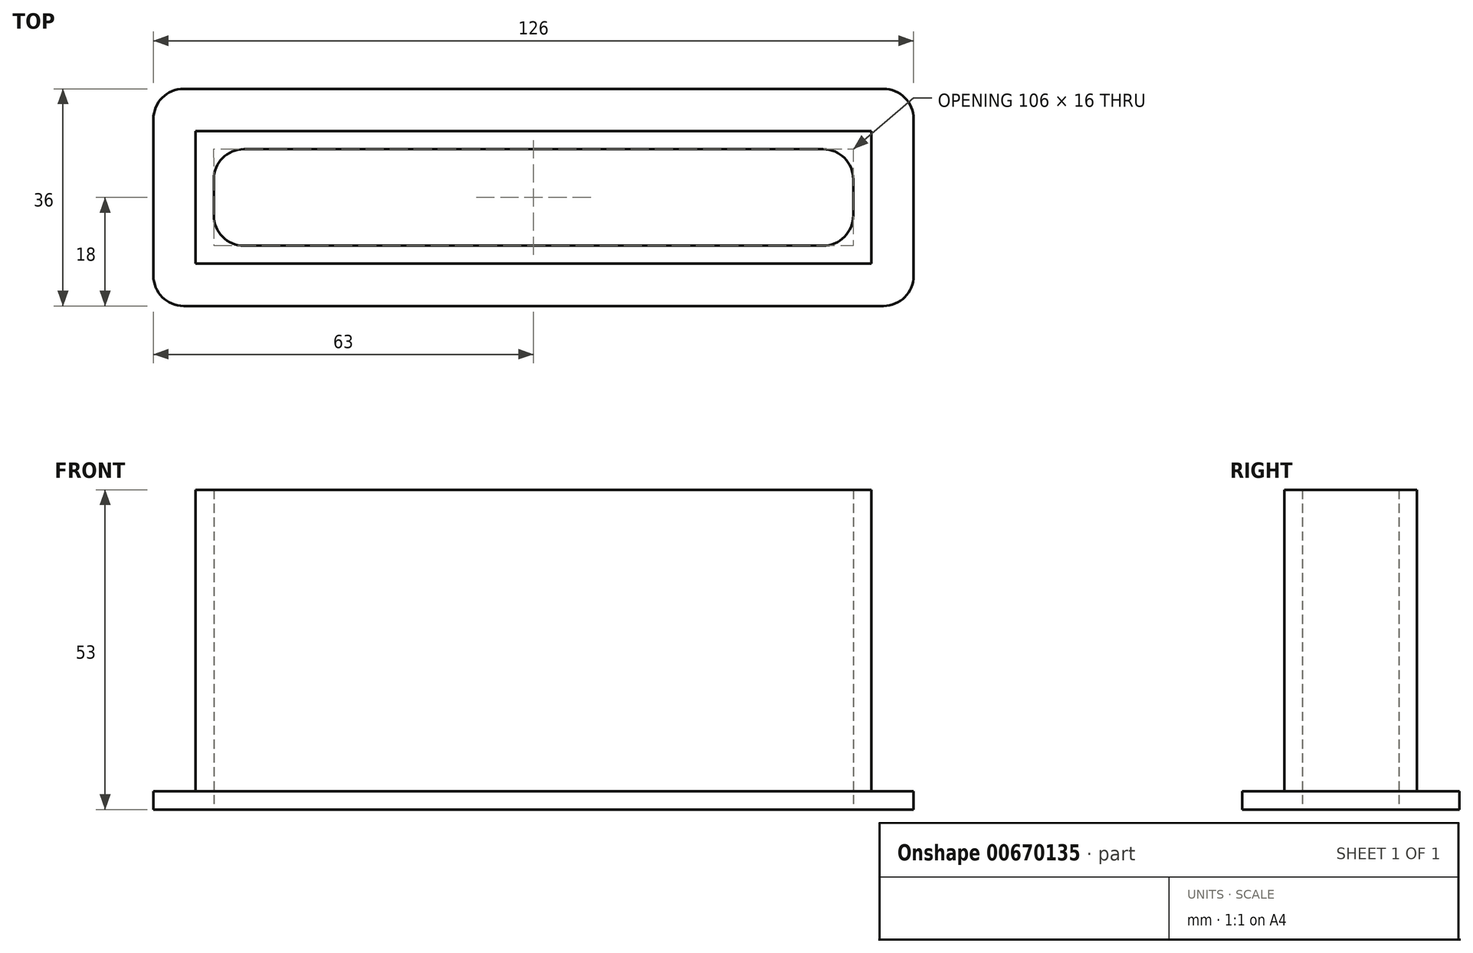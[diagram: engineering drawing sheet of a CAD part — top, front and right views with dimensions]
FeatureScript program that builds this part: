
annotation { "Feature Type Name" : "Feature", "Feature Type Description" : "" }
export const myFeature = defineFeature(function(context is Context, id is Id, definition is map)
    precondition{}
    {
        {
            var Q0;
            Q0=qCreatedBy(makeId("Top.planeOp"),FACE);
            var sketch = newSketch(context, id + "F0", { "sketchPlane" : qUnion([Q0])});
            skLineSegment(sketch, "E0.bottom", {"start": v(0, 0) * mm, "end": v(-106, 0) * mm});
            skLineSegment(sketch, "E0.top", {"start": v(0, 16) * mm, "end": v(-106, 16) * mm});
            skLineSegment(sketch, "E0.left", {"start": v(0, 0) * mm, "end": v(0, 16) * mm});
            skLineSegment(sketch, "E0.right", {"start": v(-106, 0) * mm, "end": v(-106, 16) * mm});
            skLineSegment(sketch, "E1.bottom", {"start": v(10, -10) * mm, "end": v(-116, -10) * mm});
            skLineSegment(sketch, "E1.top", {"start": v(10, 26) * mm, "end": v(-116, 26) * mm});
            skLineSegment(sketch, "E1.left", {"start": v(10, -10) * mm, "end": v(10, 26) * mm});
            skLineSegment(sketch, "E1.right", {"start": v(-116, -10) * mm, "end": v(-116, 26) * mm});
            skSolve(sketch);
        }
        {
            var Q0;
            Q0 = qSketchRegion(id + "F0", true);
            extrude(context, id + "F1", {"entities" : qUnion([Q0]), "depth" : 3 * mm, "offsetDistance" : 25 * mm});
        }
        {
            var Q0;
            Q0=makeQuery(id+"F1.opExtrude","CAP_FACE",FACE,{"disambiguationData":[OSD([sQuery(id+"F0.wireOp",EDGE,"E0.bottom"),sQuery(id+"F0.wireOp",EDGE,"E0.top"),sQuery(id+"F0.wireOp",EDGE,"E0.left"),sQuery(id+"F0.wireOp",EDGE,"E0.right"),sQuery(id+"F0.wireOp",EDGE,"E1.bottom"),sQuery(id+"F0.wireOp",EDGE,"E1.top"),sQuery(id+"F0.wireOp",EDGE,"E1.left"),sQuery(id+"F0.wireOp",EDGE,"E1.right")])],"isStart":false});
            var sketch = newSketch(context, id + "F2", { "sketchPlane" : qUnion([Q0])});
            skLineSegment(sketch, "E2.bottom", {"start": v(-106, 16) * mm, "end": v(0, 16) * mm});
            skLineSegment(sketch, "E2.top", {"start": v(-106, 0) * mm, "end": v(0, 0) * mm});
            skLineSegment(sketch, "E2.left", {"start": v(-106, 16) * mm, "end": v(-106, 0) * mm});
            skLineSegment(sketch, "E2.right", {"start": v(0, 16) * mm, "end": v(0, 0) * mm});
            skLineSegment(sketch, "E3.0", {"start": v(-109, 19) * mm, "end": v(3, 19) * mm});
            skLineSegment(sketch, "E3.1", {"start": v(-109, 19) * mm, "end": v(-109, -3) * mm});
            skLineSegment(sketch, "E3.2", {"start": v(-109, -3) * mm, "end": v(3, -3) * mm});
            skLineSegment(sketch, "E3.3", {"start": v(3, 19) * mm, "end": v(3, -3) * mm});
            skSolve(sketch);
        }
        {
            var Q0;
            Q0 = qSketchRegion(id + "F2", true);
            extrude(context, id + "F3", {"entities" : qUnion([Q0]), "operationType" : NewBodyOperationType.ADD, "depth" : 50 * mm, "offsetDistance" : 25 * mm});
        }
        {
            var Q0;
            Q0=makeQuery(id+"F1.opExtrude","SWEPT_EDGE",EDGE,{"disambiguationData":[OSD([sQuery(id+"F0.wireOp",EDGE,"E1.top"),sQuery(id+"F0.wireOp",EDGE,"E1.right")])]});
            var Q1;
            Q1=makeQuery(id+"F1.opExtrude","SWEPT_EDGE",EDGE,{"disambiguationData":[OSD([sQuery(id+"F0.wireOp",EDGE,"E1.top"),sQuery(id+"F0.wireOp",EDGE,"E1.left")])]});
            var Q2;
            Q2=makeQuery(id+"F1.opExtrude","SWEPT_EDGE",EDGE,{"disambiguationData":[OSD([sQuery(id+"F0.wireOp",EDGE,"E1.bottom"),sQuery(id+"F0.wireOp",EDGE,"E1.left")])]});
            var Q3;
            Q3=makeQuery(id+"F1.opExtrude","SWEPT_EDGE",EDGE,{"disambiguationData":[OSD([sQuery(id+"F0.wireOp",EDGE,"E1.bottom"),sQuery(id+"F0.wireOp",EDGE,"E1.right")])]});
            var Q4;
            Q4=makeQuery(id+"F3.boolean.opBoolean","MERGE",EDGE,{"derivedFrom":[makeQuery(id+"F1.opExtrude","SWEPT_EDGE",EDGE,{"disambiguationData":[OSD([sQuery(id+"F0.wireOp",EDGE,"E0.top"),sQuery(id+"F0.wireOp",EDGE,"E0.right")])]}),makeQuery(id+"F3.opExtrude","SWEPT_EDGE",EDGE,{"disambiguationData":[OSD([sQuery(id+"F2.wireOp",EDGE,"E2.bottom"),sQuery(id+"F2.wireOp",EDGE,"E2.left")])]})]});
            var Q5;
            Q5=makeQuery(id+"F3.boolean.opBoolean","MERGE",EDGE,{"derivedFrom":[makeQuery(id+"F1.opExtrude","SWEPT_EDGE",EDGE,{"disambiguationData":[OSD([sQuery(id+"F0.wireOp",EDGE,"E0.top"),sQuery(id+"F0.wireOp",EDGE,"E0.left")])]}),makeQuery(id+"F3.opExtrude","SWEPT_EDGE",EDGE,{"disambiguationData":[OSD([sQuery(id+"F2.wireOp",EDGE,"E2.bottom"),sQuery(id+"F2.wireOp",EDGE,"E2.right")])]})]});
            var Q6;
            Q6=makeQuery(id+"F3.boolean.opBoolean","MERGE",EDGE,{"derivedFrom":[makeQuery(id+"F1.opExtrude","SWEPT_EDGE",EDGE,{"disambiguationData":[OSD([sQuery(id+"F0.wireOp",EDGE,"E0.bottom"),sQuery(id+"F0.wireOp",EDGE,"E0.left")])]}),makeQuery(id+"F3.opExtrude","SWEPT_EDGE",EDGE,{"disambiguationData":[OSD([sQuery(id+"F2.wireOp",EDGE,"E2.top"),sQuery(id+"F2.wireOp",EDGE,"E2.right")])]})]});
            var Q7;
            Q7=makeQuery(id+"F3.boolean.opBoolean","MERGE",EDGE,{"derivedFrom":[makeQuery(id+"F1.opExtrude","SWEPT_EDGE",EDGE,{"disambiguationData":[OSD([sQuery(id+"F0.wireOp",EDGE,"E0.bottom"),sQuery(id+"F0.wireOp",EDGE,"E0.right")])]}),makeQuery(id+"F3.opExtrude","SWEPT_EDGE",EDGE,{"disambiguationData":[OSD([sQuery(id+"F2.wireOp",EDGE,"E2.top"),sQuery(id+"F2.wireOp",EDGE,"E2.left")])]})]});
            fillet(context, id + "F4", {"entities" : qUnion([Q0, Q1, Q2, Q3, Q4, Q5, Q6, Q7]), "radius" : 5 * mm, "tangentPropagation" : true, "allowEdgeOverflow" : false});
        }
    });
